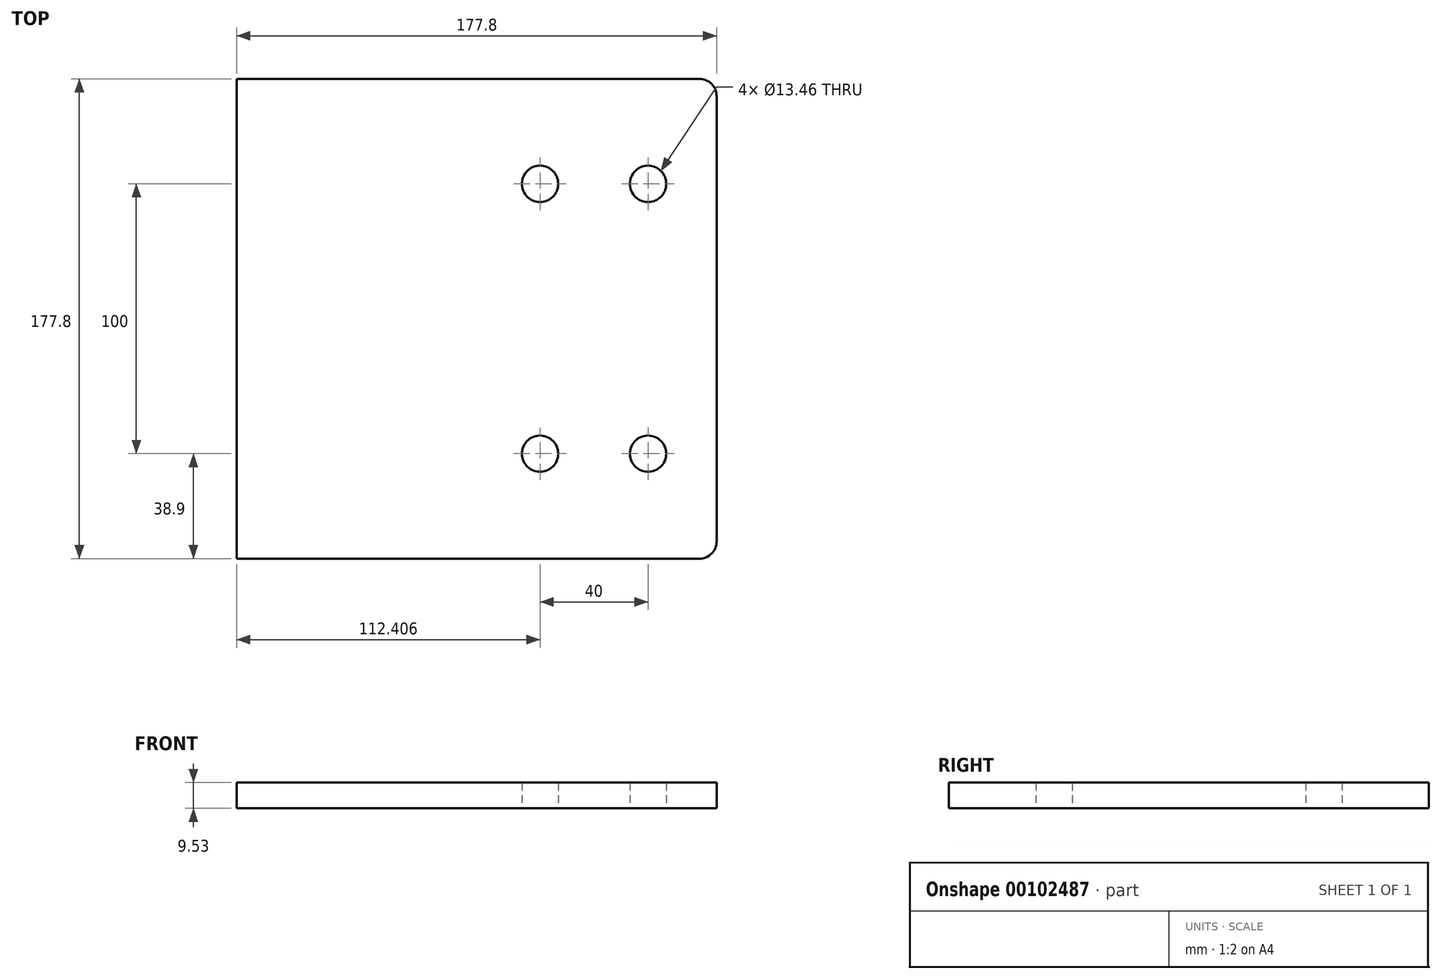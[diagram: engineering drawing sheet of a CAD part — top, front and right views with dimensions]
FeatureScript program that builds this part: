
annotation { "Feature Type Name" : "Feature", "Feature Type Description" : "" }
export const myFeature = defineFeature(function(context is Context, id is Id, definition is map)
    precondition{}
    {
        {
            var Q0;
            Q0=qCreatedBy(makeId("Top.planeOp"),FACE);
            var sketch = newSketch(context, id + "F0", { "sketchPlane" : qUnion([Q0])});
            skLineSegment(sketch, "E0", {"start": v(88.9, -82.55) * mm, "end": v(88.9, 82.55) * mm});
            skLineSegment(sketch, "E1", {"start": v(-88.9, 88.9) * mm, "end": v(82.55, 88.9) * mm});
            skLineSegment(sketch, "E2", {"start": v(-88.9, -88.9) * mm, "end": v(82.55, -88.9) * mm});
            skArc(sketch, "E3", {"start": v(88.9, 82.55) * mm, "mid": v(87.04, 87.04) * mm, "end": v(82.55, 88.9) * mm});
            skArc(sketch, "E4", {"start": v(82.55, -88.9) * mm, "mid": v(87.04, -87.04) * mm, "end": v(88.9, -82.55) * mm});
            skLineSegment(sketch, "E5", {"start": v(-88.9, 88.9) * mm, "end": v(-88.9, -88.9) * mm});
            skCircle(sketch, "E6", {"center": v(63.5, -50) * mm, "radius": 6.73 * mm});
            skCircle(sketch, "E7", {"center": v(23.5, -50) * mm, "radius": 6.73 * mm});
            skCircle(sketch, "E8", {"center": v(23.5, 50) * mm, "radius": 6.73 * mm});
            skCircle(sketch, "E9", {"center": v(63.5, 50) * mm, "radius": 6.73 * mm});
            skSolve(sketch);
        }
        {
            var Q0;
            Q0 = qSketchRegion(id + "F0", true);
            extrude(context, id + "F1", {"entities" : qUnion([Q0]), "depth" : 9.52 * mm});
        }
    });
